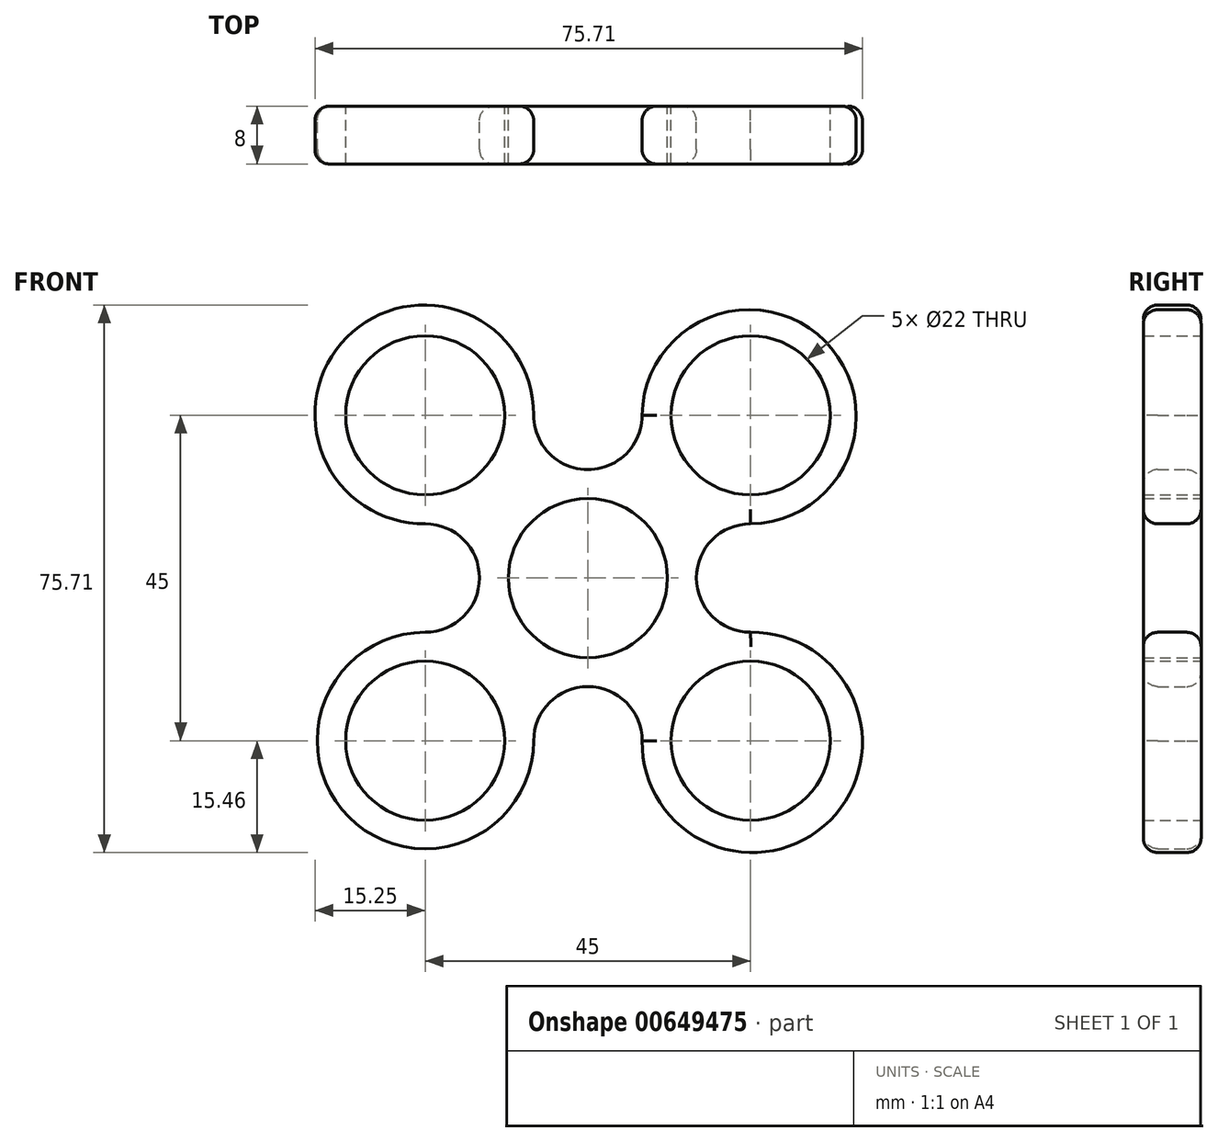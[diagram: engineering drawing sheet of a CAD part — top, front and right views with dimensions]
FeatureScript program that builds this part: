
annotation { "Feature Type Name" : "Feature", "Feature Type Description" : "" }
export const myFeature = defineFeature(function(context is Context, id is Id, definition is map)
    precondition{}
    {
        {
            var Q0;
            Q0=qCreatedBy(makeId("Front.planeOp"),FACE);
            var sketch = newSketch(context, id + "F0", { "sketchPlane" : qUnion([Q0])});
            skCircle(sketch, "E0", {"center": v(0, 0) * mm, "radius": 11 * mm});
            skCircle(sketch, "E1", {"center": v(-22.5, -22.5) * mm, "radius": 11 * mm});
            skCircle(sketch, "E2", {"center": v(-22.5, 22.5) * mm, "radius": 11 * mm});
            skCircle(sketch, "E3", {"center": v(22.5, 22.5) * mm, "radius": 11 * mm});
            skCircle(sketch, "E4", {"center": v(22.5, -22.5) * mm, "radius": 11 * mm});
            skArc(sketch, "E5", {"start": v(-22.5, -7.5) * mm, "mid": v(-15, 0) * mm, "end": v(-22.5, 7.5) * mm});
            skArc(sketch, "E6", {"start": v(-7.5, 22.58) * mm, "mid": v(-0.04, 15) * mm, "end": v(7.5, 22.5) * mm});
            skPoint(sketch, "E6.startSnap0", {"position": v(0, 22.5) * mm});
            skArc(sketch, "E7", {"start": v(22.5, 7.5) * mm, "mid": v(15, 0) * mm, "end": v(22.5, -7.5) * mm});
            skArc(sketch, "E8", {"start": v(7.5, -22.5) * mm, "mid": v(0, -15) * mm, "end": v(-7.5, -22.5) * mm});
            skArc(sketch, "E9", {"start": v(-22.5, -7.5) * mm, "mid": v(-33.05, -33.05) * mm, "end": v(-7.5, -22.5) * mm});
            skArc(sketch, "E10", {"start": v(7.5, -22.5) * mm, "mid": v(33.5, -33.5) * mm, "end": v(22.5, -7.5) * mm});
            skArc(sketch, "E11", {"start": v(22.5, 7.5) * mm, "mid": v(32.73, 32.82) * mm, "end": v(7.5, 22.37) * mm});
            skArc(sketch, "E12", {"start": v(-7.5, 22.5) * mm, "mid": v(-33.32, 33.32) * mm, "end": v(-22.5, 7.5) * mm});
            skSolve(sketch);
        }
        {
            var Q0;
            Q0=makeQuery(id+"F0.imprint","IMPRINT",FACE,{"disambiguationData":[TD([[makeQuery(id+"F0.imprint","IMPRINT",EDGE,{"derivedFrom":sQuery(id+"F0.wireOp",EDGE,"E0")}),-1.0]])]});
            extrude(context, id + "F1", {"entities" : qUnion([Q0]), "depth" : 8 * mm, "offsetDistance" : 25 * mm});
        }
        {
            var Q0;
            Q0=makeQuery(id+"F1.opExtrude","CAP_EDGE",EDGE,{"disambiguationData":[OSD([sQuery(id+"F0.wireOp",EDGE,"E12")])],"isStart":false});
            var Q1;
            Q1=makeQuery(id+"F1.opExtrude","CAP_EDGE",EDGE,{"disambiguationData":[OSD([sQuery(id+"F0.wireOp",EDGE,"E6")])],"isStart":false});
            var Q2;
            Q2=makeQuery(id+"F1.opExtrude","CAP_EDGE",EDGE,{"disambiguationData":[OSD([sQuery(id+"F0.wireOp",EDGE,"E11")])],"isStart":false});
            var Q3;
            Q3=makeQuery(id+"F1.opExtrude","CAP_EDGE",EDGE,{"disambiguationData":[OSD([sQuery(id+"F0.wireOp",EDGE,"E7")])],"isStart":false});
            var Q4;
            Q4=makeQuery(id+"F1.opExtrude","CAP_EDGE",EDGE,{"disambiguationData":[OSD([sQuery(id+"F0.wireOp",EDGE,"E10")])],"isStart":false});
            var Q5;
            Q5=makeQuery(id+"F1.opExtrude","CAP_EDGE",EDGE,{"disambiguationData":[OSD([sQuery(id+"F0.wireOp",EDGE,"E8")])],"isStart":false});
            var Q6;
            Q6=makeQuery(id+"F1.opExtrude","CAP_EDGE",EDGE,{"disambiguationData":[OSD([sQuery(id+"F0.wireOp",EDGE,"E9")])],"isStart":false});
            var Q7;
            Q7=makeQuery(id+"F1.opExtrude","CAP_EDGE",EDGE,{"disambiguationData":[OSD([sQuery(id+"F0.wireOp",EDGE,"E5")])],"isStart":false});
            fillet(context, id + "F2", {"entities" : qUnion([Q0, Q1, Q2, Q3, Q4, Q5, Q6, Q7]), "radius" : 2 * mm, "tangentPropagation" : true, "allowEdgeOverflow" : false});
        }
        {
            var Q0;
            Q0=makeQuery(id+"F1.opExtrude","CAP_EDGE",EDGE,{"disambiguationData":[OSD([sQuery(id+"F0.wireOp",EDGE,"E11")])],"isStart":true});
            var Q1;
            Q1=makeQuery(id+"F1.opExtrude","CAP_EDGE",EDGE,{"disambiguationData":[OSD([sQuery(id+"F0.wireOp",EDGE,"E6")])],"isStart":true});
            var Q2;
            Q2=makeQuery(id+"F1.opExtrude","CAP_EDGE",EDGE,{"disambiguationData":[OSD([sQuery(id+"F0.wireOp",EDGE,"E12")])],"isStart":true});
            var Q3;
            Q3=makeQuery(id+"F1.opExtrude","CAP_EDGE",EDGE,{"disambiguationData":[OSD([sQuery(id+"F0.wireOp",EDGE,"E7")])],"isStart":true});
            var Q4;
            Q4=makeQuery(id+"F1.opExtrude","CAP_EDGE",EDGE,{"disambiguationData":[OSD([sQuery(id+"F0.wireOp",EDGE,"E5")])],"isStart":true});
            var Q5;
            Q5=makeQuery(id+"F1.opExtrude","CAP_EDGE",EDGE,{"disambiguationData":[OSD([sQuery(id+"F0.wireOp",EDGE,"E9")])],"isStart":true});
            var Q6;
            Q6=makeQuery(id+"F1.opExtrude","CAP_EDGE",EDGE,{"disambiguationData":[OSD([sQuery(id+"F0.wireOp",EDGE,"E8")])],"isStart":true});
            var Q7;
            Q7=makeQuery(id+"F1.opExtrude","CAP_EDGE",EDGE,{"disambiguationData":[OSD([sQuery(id+"F0.wireOp",EDGE,"E10")])],"isStart":true});
            fillet(context, id + "F3", {"entities" : qUnion([Q0, Q1, Q2, Q3, Q4, Q5, Q6, Q7]), "radius" : 2 * mm, "tangentPropagation" : true, "allowEdgeOverflow" : false});
        }
    });
